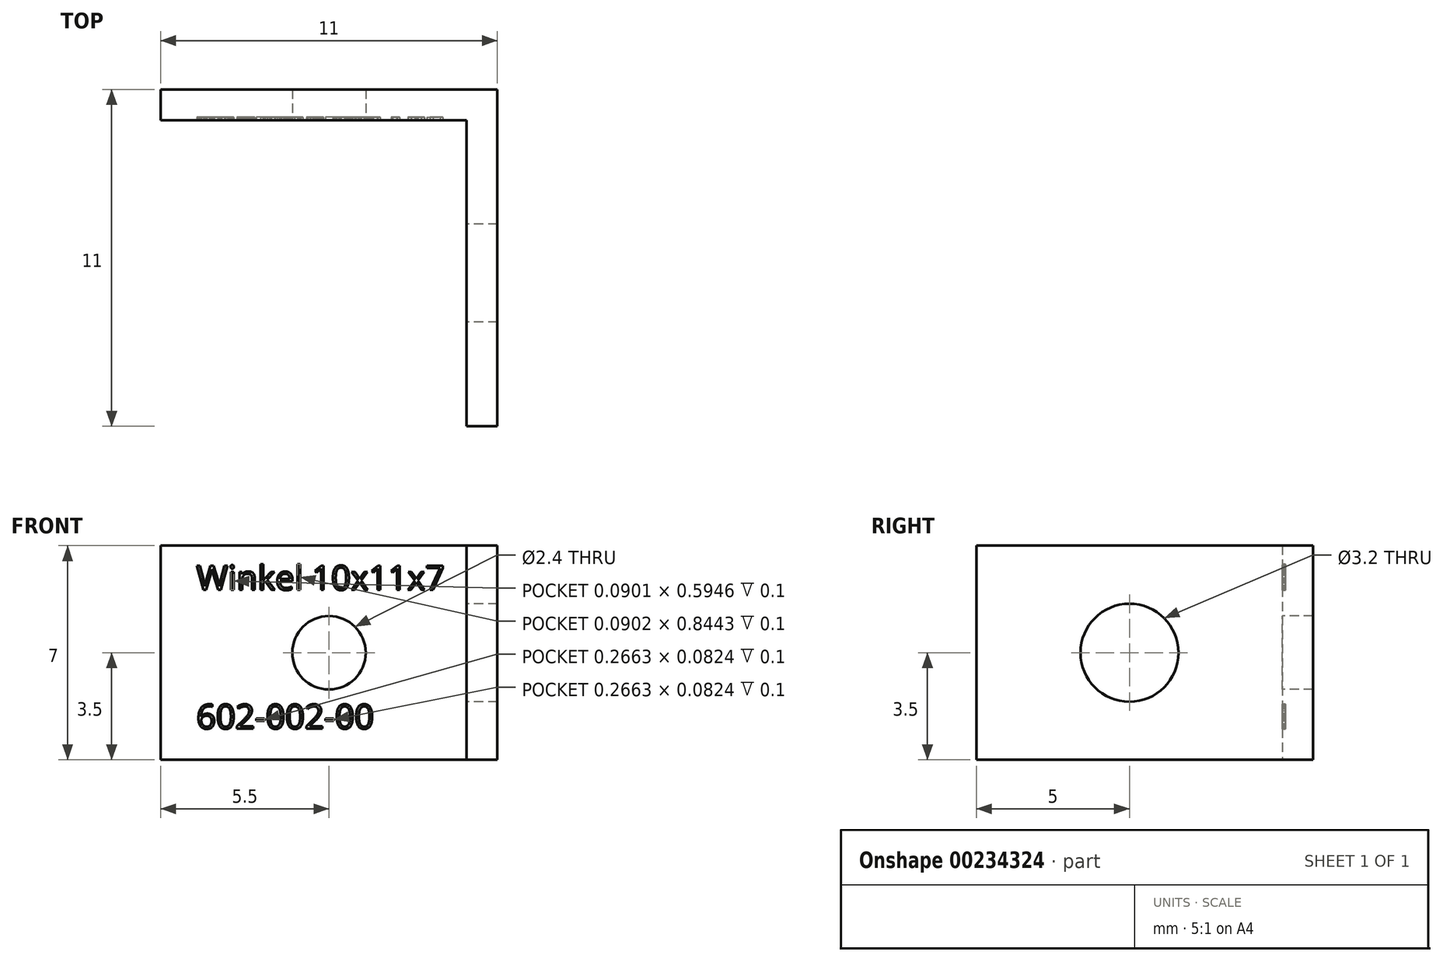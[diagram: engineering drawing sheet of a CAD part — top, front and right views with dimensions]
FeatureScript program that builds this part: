
annotation { "Feature Type Name" : "Feature", "Feature Type Description" : "" }
export const myFeature = defineFeature(function(context is Context, id is Id, definition is map)
    precondition{}
    {
        {
            var Q0;
            Q0=qCreatedBy(makeId("Front.planeOp"),FACE);
            var sketch = newSketch(context, id + "F0", { "sketchPlane" : qUnion([Q0])});
            skLineSegment(sketch, "E0.bottom", {"start": v(-5.5, 3.5) * mm, "end": v(5.5, 3.5) * mm});
            skLineSegment(sketch, "E0.top", {"start": v(-5.5, -3.5) * mm, "end": v(5.5, -3.5) * mm});
            skLineSegment(sketch, "E0.left", {"start": v(-5.5, 3.5) * mm, "end": v(-5.5, -3.5) * mm});
            skLineSegment(sketch, "E0.right", {"start": v(5.5, 3.5) * mm, "end": v(5.5, -3.5) * mm});
            skCircle(sketch, "E1", {"center": v(0, 0) * mm, "radius": 1.2 * mm});
            skLineSegment(sketch, "E2", {"start": v(4.5, 3.5) * mm, "end": v(4.5, -3.5) * mm});
            skLineSegment(sketch, "E3", {"start": v(-5.5, 0) * mm, "end": v(5.5, 0) * mm, "construction": true});
            skLineSegment(sketch, "E4", {"start": v(0, 3.5) * mm, "end": v(0, -3.5) * mm, "construction": true});
            skSolve(sketch);
        }
        {
            var Q0;
            {var subQ0=sQuery(id+"F0.wireOp",EDGE,"E0.left");Q0=makeQuery(id+"F0.imprint","IMPRINT",FACE,{"disambiguationData":[TD([[makeQuery(id+"F0.imprint","IMPRINT",EDGE,{"derivedFrom":subQ0}),1.0]])]});}
            var Q1;
            {var subQ0=sQuery(id+"F0.wireOp",EDGE,"E0.right");Q1=makeQuery(id+"F0.imprint","IMPRINT",FACE,{"disambiguationData":[TD([[makeQuery(id+"F0.imprint","IMPRINT",EDGE,{"derivedFrom":subQ0}),-1.0]])]});}
            extrude(context, id + "F1", {"entities" : qUnion([Q0, Q1]), "oppositeDirection" : true, "depth" : 1 * mm});
        }
        {
            var Q0;
            {var subQ0=sQuery(id+"F0.wireOp",EDGE,"E0.right");Q0=makeQuery(id+"F0.imprint","IMPRINT",FACE,{"disambiguationData":[TD([[makeQuery(id+"F0.imprint","IMPRINT",EDGE,{"derivedFrom":subQ0}),-1.0]])]});}
            extrude(context, id + "F2", {"entities" : qUnion([Q0]), "operationType" : NewBodyOperationType.ADD, "depth" : 10 * mm});
        }
        {
            var Q0;
            Q0=makeQuery(id+"F2.opExtrude","SWEPT_FACE",FACE,{"disambiguationData":[OSD([sQuery(id+"F0.wireOp",EDGE,"E2")])]});
            var sketch = newSketch(context, id + "F3", { "sketchPlane" : qUnion([Q0])});
            skCircle(sketch, "E5", {"center": v(5, 0) * mm, "radius": 1.6 * mm});
            skPoint(sketch, "E5.centerSnap0", {"position": v(10, 0) * mm});
            skPoint(sketch, "E5.centerSnap1", {"position": v(5, 3.5) * mm});
            skSolve(sketch);
        }
        {
            var Q0;
            Q0=makeQuery(id+"F3.imprint","IMPRINT",FACE,{"disambiguationData":[TD([[makeQuery(id+"F3.imprint","IMPRINT",EDGE,{"derivedFrom":sQuery(id+"F3.wireOp",EDGE,"E5")}),1.0]])]});
            extrude(context, id + "F4", {"entities" : qUnion([Q0]), "operationType" : NewBodyOperationType.REMOVE, "endBound" : BoundingType.UP_TO_NEXT, "oppositeDirection" : true, "depth" : 25 * mm});
        }
        {
            var Q0;
            Q0=makeQuery(id+"F1.opExtrude","CAP_FACE",FACE,{"disambiguationData":[OSD([sQuery(id+"F0.wireOp",EDGE,"E0.bottom"),sQuery(id+"F0.wireOp",EDGE,"E0.top"),sQuery(id+"F0.wireOp",EDGE,"E0.left"),sQuery(id+"F0.wireOp",EDGE,"E0.right"),sQuery(id+"F0.wireOp",EDGE,"E1")])],"isStart":true});
            var sketch = newSketch(context, id + "F5", { "sketchPlane" : qUnion([Q0])});
            skText(sketch, "E6", { "text": "Winkel 10x11x7\n\n\n602-002-00", "fontName": "OpenSans-Regular.ttf"});
            const initialGuessF5  = {"E6": [-0.00433, 0.00205, 1, 0, 0.0008]};
            skSetInitialGuess(sketch, initialGuessF5);
            skSolve(sketch);
        }
        {
            var Q0;
            Q0 = qSketchRegion(id + "F5", true);
            extrude(context, id + "F6", {"entities" : qUnion([Q0]), "operationType" : NewBodyOperationType.REMOVE, "oppositeDirection" : true, "depth" : .1 * mm});
        }
    });
